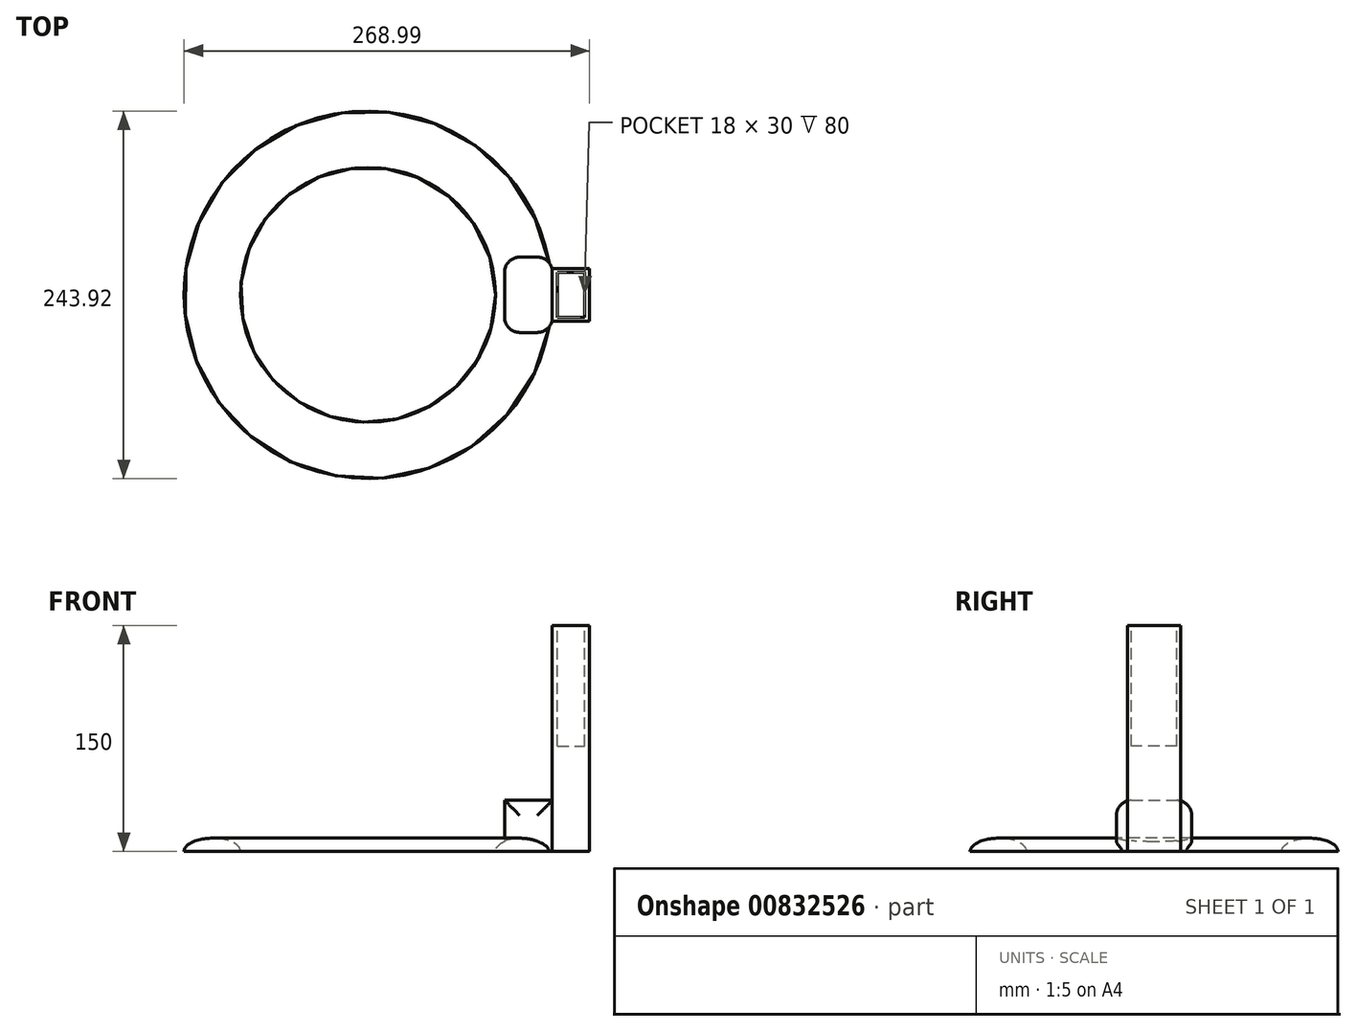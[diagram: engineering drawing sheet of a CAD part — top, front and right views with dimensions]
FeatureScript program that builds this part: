
annotation { "Feature Type Name" : "Feature", "Feature Type Description" : "" }
export const myFeature = defineFeature(function(context is Context, id is Id, definition is map)
    precondition{}
    {
        {
            var Q0;
            Q0=qCreatedBy(makeId("Front.planeOp"),FACE);
            var sketch = newSketch(context, id + "F0", { "sketchPlane" : qUnion([Q0])});
            skEllipticalArc(sketch, "E0", {});
            skLineSegment(sketch, "E1", {"start": v(-12.35, 0) * mm, "end": v(39.89, 0) * mm});
            skLineSegment(sketch, "E2", {"start": v(-90.63, 43.97) * mm, "end": v(-90.63, -51) * mm});
            const initialGuessF0  = {"E0": [0.012610239265822415, 0, 1, 0, 0.018715491595103412, 0.008907713994841755, 0, 3.141592653589793]};
            skSetInitialGuess(sketch, initialGuessF0);
            skSolve(sketch);
        }
        {
            var Q0;
            {var subQ0=sQuery(id+"F0.wireOp",EDGE,"E0");Q0=makeQuery(id+"F0.imprint","IMPRINT",FACE,{"disambiguationData":[TD([[makeQuery(id+"F0.imprint","IMPRINT",EDGE,{"derivedFrom":subQ0}),1.0]])]});}
            var Q1;
            Q1=sQuery(id+"F0.wireOp",EDGE,"E2");
            revolve(context, id + "F1", {"surfaceOperationType" : NewSurfaceOperationType.NEW, "entities" : qUnion([Q0]), "axis" : qUnion([Q1]), "revolveType" : RevolveType.FULL});
        }
        {
            var Q0;
            Q0=qCreatedBy(makeId("Right.planeOp"),FACE);
            var sketch = newSketch(context, id + "F2", { "sketchPlane" : qUnion([Q0])});
            skLineSegment(sketch, "E3.bottom", {"start": v(-25, 33.99) * mm, "end": v(25, 33.99) * mm});
            skLineSegment(sketch, "E3.top", {"start": v(-25, 0) * mm, "end": v(25, 0) * mm});
            skLineSegment(sketch, "E3.left", {"start": v(-25, 33.99) * mm, "end": v(-25, 0) * mm});
            skLineSegment(sketch, "E3.right", {"start": v(25, 33.99) * mm, "end": v(25, 0) * mm});
            skSolve(sketch);
        }
        {
            var Q0;
            Q0=makeQuery(id+"F2.imprint","IMPRINT",FACE,{"disambiguationData":[TD([[makeQuery(id+"F2.imprint","IMPRINT",EDGE,{"derivedFrom":sQuery(id+"F2.wireOp",EDGE,"E3.bottom")}),-1.0]])]});
            extrude(context, id + "F3", {"entities" : qUnion([Q0]), "operationType" : NewBodyOperationType.ADD, "depth" : 31.4 * mm, "offsetDistance" : 25 * mm});
        }
        {
            var Q0;
            Q0=makeQuery(id+"F3.opExtrude","CAP_FACE",FACE,{"disambiguationData":[OSD([sQuery(id+"F2.wireOp",EDGE,"E3.bottom"),sQuery(id+"F2.wireOp",EDGE,"E3.top"),sQuery(id+"F2.wireOp",EDGE,"E3.left"),sQuery(id+"F2.wireOp",EDGE,"E3.right")])],"isStart":false});
            var sketch = newSketch(context, id + "F4", { "sketchPlane" : qUnion([Q0])});
            skLineSegment(sketch, "E4.bottom", {"start": v(-17.5, 150) * mm, "end": v(17.5, 150) * mm});
            skLineSegment(sketch, "E4.top", {"start": v(-17.5, 0) * mm, "end": v(17.5, 0) * mm});
            skLineSegment(sketch, "E4.left", {"start": v(-17.5, 150) * mm, "end": v(-17.5, 0) * mm});
            skLineSegment(sketch, "E4.right", {"start": v(17.5, 150) * mm, "end": v(17.5, 0) * mm});
            skSolve(sketch);
        }
        {
            var Q0;
            {var subQ0=sQuery(id+"F4.wireOp",EDGE,"E4.top");Q0=makeQuery(id+"F4.imprint","IMPRINT",FACE,{"disambiguationData":[TD([[makeQuery(id+"F4.imprint","IMPRINT",EDGE,{"derivedFrom":subQ0}),1.0]])]});}
            var Q1;
            {var subQ0=sQuery(id+"F4.wireOp",EDGE,"E4.bottom");Q1=makeQuery(id+"F4.imprint","IMPRINT",FACE,{"disambiguationData":[TD([[makeQuery(id+"F4.imprint","IMPRINT",EDGE,{"derivedFrom":subQ0}),-1.0]])]});}
            extrude(context, id + "F5", {"entities" : qUnion([Q0, Q1]), "operationType" : NewBodyOperationType.ADD, "depth" : 25 * mm, "offsetDistance" : 25 * mm});
        }
        {
            var Q0;
            Q0=makeQuery(id+"F5.opExtrude","SWEPT_FACE",FACE,{"disambiguationData":[OSD([sQuery(id+"F4.wireOp",EDGE,"E4.bottom")])]});
            var sketch = newSketch(context, id + "F6", { "sketchPlane" : qUnion([Q0])});
            skLineSegment(sketch, "E5.bottom", {"start": v(35.02, 15) * mm, "end": v(53.02, 15) * mm});
            skLineSegment(sketch, "E5.top", {"start": v(35.02, -15) * mm, "end": v(53.02, -15) * mm});
            skLineSegment(sketch, "E5.left", {"start": v(35.02, 15) * mm, "end": v(35.02, -15) * mm});
            skLineSegment(sketch, "E5.right", {"start": v(53.02, 15) * mm, "end": v(53.02, -15) * mm});
            skSolve(sketch);
        }
        {
            var Q0;
            Q0 = qSketchRegion(id + "F6", true);
            extrude(context, id + "F7", {"entities" : qUnion([Q0]), "operationType" : NewBodyOperationType.REMOVE, "oppositeDirection" : true, "depth" : 80 * mm, "offsetDistance" : 25 * mm});
        }
        {
            var Q0;
            Q0=makeQuery(id+"F3.opExtrude","SWEPT_EDGE",EDGE,{"disambiguationData":[OSD([sQuery(id+"F2.wireOp",EDGE,"E3.bottom"),sQuery(id+"F2.wireOp",EDGE,"E3.right")])]});
            var Q1;
            Q1=makeQuery(id+"F3.opExtrude","SWEPT_EDGE",EDGE,{"disambiguationData":[OSD([sQuery(id+"F2.wireOp",EDGE,"E3.bottom"),sQuery(id+"F2.wireOp",EDGE,"E3.left")])]});
            var Q2;
            Q2=makeQuery(id+"F3.opExtrude","CAP_EDGE",EDGE,{"disambiguationData":[OSD([sQuery(id+"F2.wireOp",EDGE,"E3.left")])],"isStart":true});
            var Q3;
            Q3=makeQuery(id+"F3.opExtrude","CAP_EDGE",EDGE,{"disambiguationData":[OSD([sQuery(id+"F2.wireOp",EDGE,"E3.right")])],"isStart":true});
            fillet(context, id + "F8", {"entities" : qUnion([Q0, Q1, Q2, Q3]), "radius" : 10 * mm, "tangentPropagation" : true, "allowEdgeOverflow" : false});
        }
        {
            var Q0;
            Q0=makeQuery(id+"F3.opExtrude","CAP_EDGE",EDGE,{"disambiguationData":[OSD([sQuery(id+"F2.wireOp",EDGE,"E3.right")])],"isStart":false});
            var Q1;
            Q1=makeQuery(id+"F3.opExtrude","CAP_EDGE",EDGE,{"disambiguationData":[OSD([sQuery(id+"F2.wireOp",EDGE,"E3.left")])],"isStart":false});
            fillet(context, id + "F9", {"entities" : qUnion([Q0, Q1]), "radius" : 10 * mm, "tangentPropagation" : true, "allowEdgeOverflow" : false});
        }
    });
